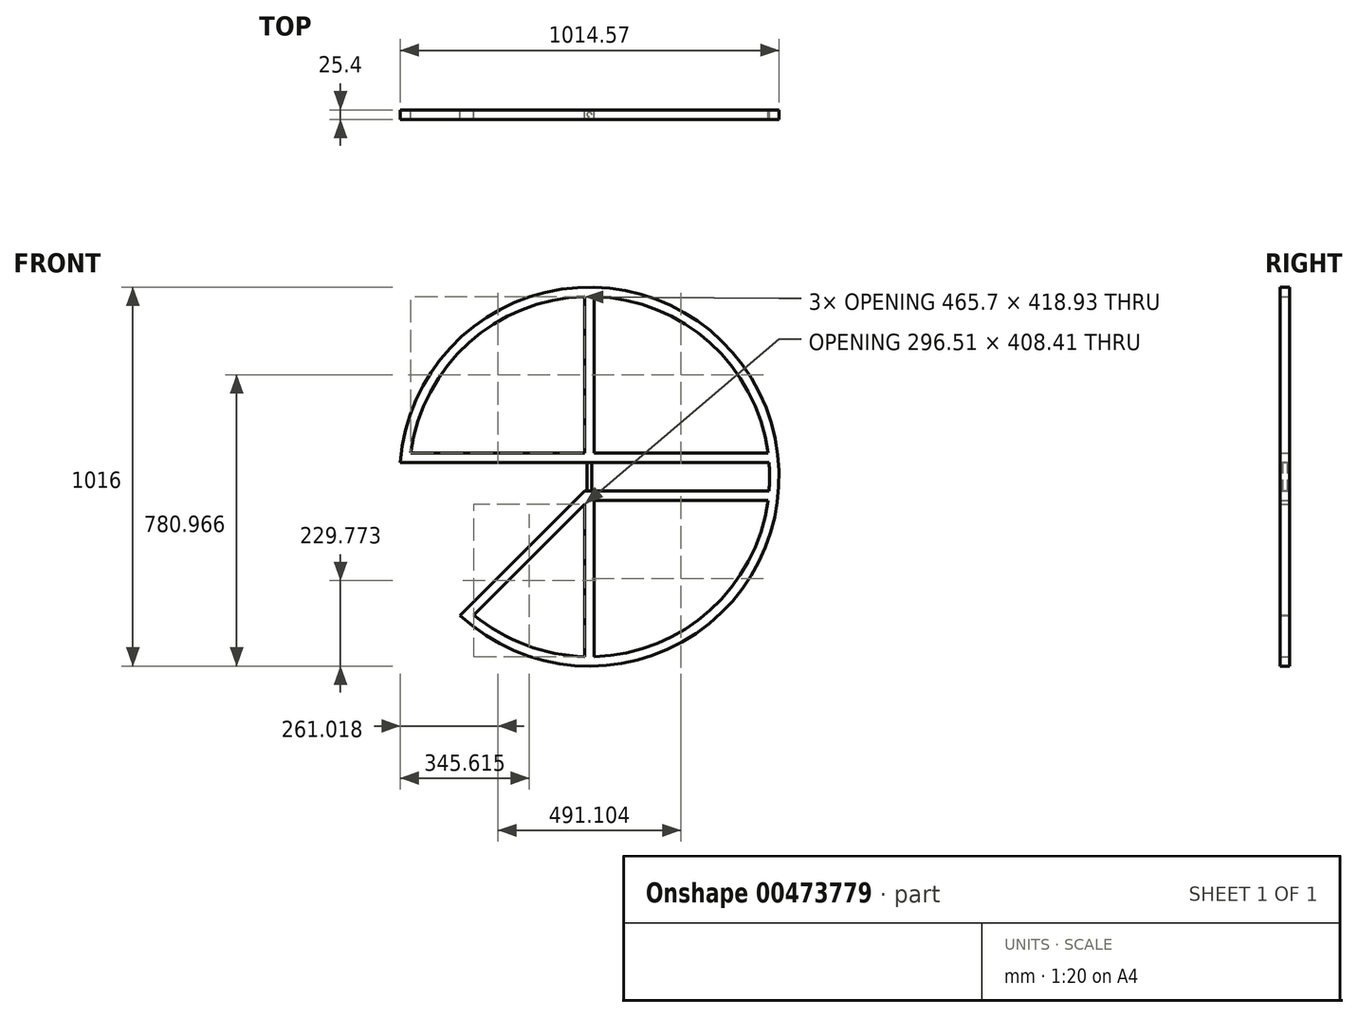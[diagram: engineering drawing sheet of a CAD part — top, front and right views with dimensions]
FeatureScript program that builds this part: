
annotation { "Feature Type Name" : "Feature", "Feature Type Description" : "" }
export const myFeature = defineFeature(function(context is Context, id is Id, definition is map)
    precondition{}
    {
        {
            var Q0;
            Q0=qCreatedBy(makeId("Front.planeOp"),FACE);
            var sketch = newSketch(context, id + "F0", { "sketchPlane" : qUnion([Q0])});
            skArc(sketch, "E0", {"start": v(-346.29, -371.69) * mm, "mid": v(473.1, 185.05) * mm, "end": v(-506.57, 38.1) * mm});
            skArc(sketch, "E1", {"start": v(-12.7, 482.43) * mm, "mid": v(-322.76, 358.8) * mm, "end": v(-478.4, 63.5) * mm});
            skLineSegment(sketch, "E2", {"start": v(-12.7, 482.43) * mm, "end": v(-12.7, 63.5) * mm});
            skLineSegment(sketch, "E3", {"start": v(12.7, 482.43) * mm, "end": v(12.7, 63.5) * mm});
            skArc(sketch, "E4.trimOffspring", {"start": v(12.7, -482.43) * mm, "mid": v(322.76, -358.8) * mm, "end": v(478.4, -63.5) * mm});
            skLineSegment(sketch, "E5", {"start": v(-506.57, 38.1) * mm, "end": v(-12.7, 38.1) * mm});
            skLineSegment(sketch, "E6", {"start": v(-478.4, 63.5) * mm, "end": v(-12.7, 63.5) * mm});
            skArc(sketch, "E7.trimOffspring", {"start": v(478.4, 63.5) * mm, "mid": v(322.76, 358.8) * mm, "end": v(12.7, 482.43) * mm});
            skArc(sketch, "E8.trimOffspring", {"start": v(481.1, -38.1) * mm, "mid": v(482.6, 0) * mm, "end": v(481.1, 38.1) * mm});
            skLineSegment(sketch, "E9", {"start": v(-12.7, -38.1) * mm, "end": v(-346.29, -371.69) * mm});
            skLineSegment(sketch, "E10.0", {"start": v(-12.7, -74.02) * mm, "end": v(-309.2, -370.53) * mm});
            skLineSegment(sketch, "E11.trimOffspring", {"start": v(-327.24, -388.56) * mm, "end": v(-328.33, -389.65) * mm});
            skArc(sketch, "E12.trimOffspring", {"start": v(-309.2, -370.53) * mm, "mid": v(-170.4, -451.52) * mm, "end": v(-12.7, -482.43) * mm});
            skLineSegment(sketch, "E13.trimOffspring", {"start": v(-12.7, -74.02) * mm, "end": v(-12.7, -482.43) * mm});
            skLineSegment(sketch, "E14.trimOffspring", {"start": v(12.7, -63.5) * mm, "end": v(12.7, -482.43) * mm});
            skLineSegment(sketch, "E15.trimOffspring", {"start": v(-12.7, -38.1) * mm, "end": v(481.1, -38.1) * mm});
            skLineSegment(sketch, "E16.trimOffspring", {"start": v(12.7, -63.5) * mm, "end": v(478.4, -63.5) * mm});
            skLineSegment(sketch, "E17.trimOffspring", {"start": v(12.7, 63.5) * mm, "end": v(478.4, 63.5) * mm});
            skLineSegment(sketch, "E18.trimOffspring", {"start": v(-12.7, 38.1) * mm, "end": v(481.1, 38.1) * mm});
            skSolve(sketch);
        }
        {
            var Q0;
            Q0 = qSketchRegion(id + "F0", true);
            extrude(context, id + "F1", {"entities" : qUnion([Q0]), "depth" : 25.4 * mm});
        }
        {
            var Q0;
            Q0=makeQuery(id+"F1.opExtrude","SWEPT_FACE",FACE,{"disambiguationData":[OSD([sQuery(id+"F0.wireOp",EDGE,"E15.trimOffspring")])]});
            var sketch = newSketch(context, id + "F2", { "sketchPlane" : qUnion([Q0])});
            skCircle(sketch, "E19", {"center": v(0, -12.7) * mm, "radius": 6.35 * mm});
            skSolve(sketch);
        }
        {
            var Q0;
            Q0 = qSketchRegion(id + "F2", true);
            var Q1;
            Q1=makeQuery(id+"F1.opExtrude","SWEPT_FACE",FACE,{"disambiguationData":[OSD([sQuery(id+"F0.wireOp",EDGE,"E5"),sQuery(id+"F0.wireOp",EDGE,"E18.trimOffspring")])]});
            extrude(context, id + "F3", {"entities" : qUnion([Q0]), "operationType" : NewBodyOperationType.ADD, "endBound" : BoundingType.UP_TO_SURFACE, "endBoundEntityFace" : qUnion([Q1]), "depth" : 25.4 * mm});
        }
    });
